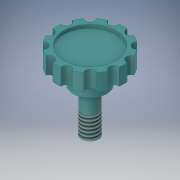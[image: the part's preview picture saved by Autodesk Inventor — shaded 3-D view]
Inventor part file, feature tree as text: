
AUTODESK INVENTOR PART (.ipt)
format: ipt  version: 2018 (Build 220112000, 112)  size: 181,248 bytes
history: native  units: in
note: dims shown in document units (in); Inventor stores cm internally (conversion verified against a paired STEP export)
features: sketch x3, hole x2, revolve x1, pattern_circular x1, thread x1
ambient origin geometry x8: Origin, YZ Plane, XZ Plane, XY Plane, X Axis, Y Axis, Z Axis, Center Point
bodies: Solid1 (feature_tree)
feature tree (8):
  revolve  "Revolution1"  [1 undecoded]
  sketch  "Sketch2"  dims[d2=0.25in d3=0.25in]
  hole  "Hole1"  [1 undecoded]
  pattern_circular  "Circular Pattern1"  [2 undecoded]
  hole  "Hole2"  [1 undecoded]
  thread  "Thread1"  [1 undecoded]
  sketch  "Sketch1"  dims[d0=1.15in d1=0.5in]
  sketch  "Sketch3"  dims[d4=0.25in d5=0.125in d6=90.0deg d7=0.78in d8=0.5in d9=15.0deg d10=0.14in d11=0.75in d12=0.375in d13=0.25in d14=0.5635in d15=1.0in d16=0.8108in d17=4.7244in d18=360.0deg d20=0.78in d21=0.75in d22=0.375in d23=0.25in d24=0.5635in d25=0.05in d26=0.0in d27=1.0in d28=0.32in]
note: 6 required parameter values undecoded (feature->parameter linkage not recoverable at this tier; creation-order binding heuristic only, values carry confidence <= 0.55)